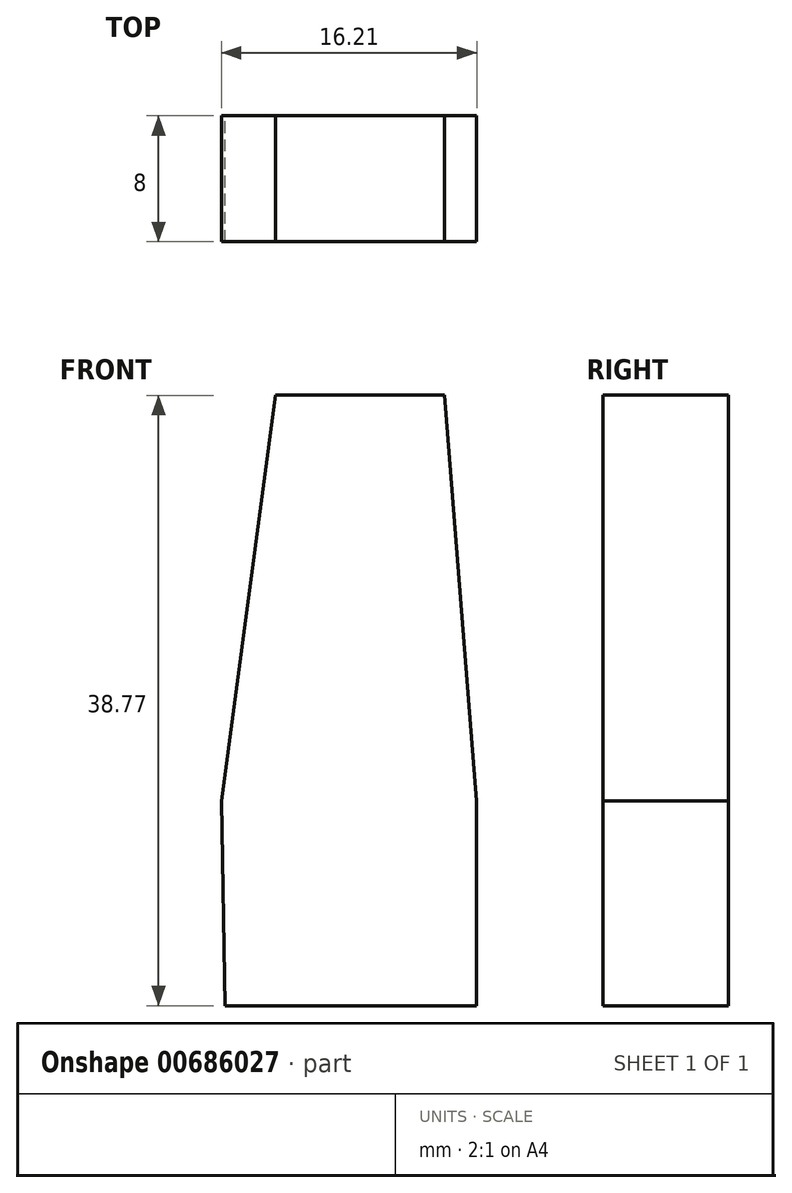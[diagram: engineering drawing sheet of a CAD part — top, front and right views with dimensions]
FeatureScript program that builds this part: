
annotation { "Feature Type Name" : "Feature", "Feature Type Description" : "" }
export const myFeature = defineFeature(function(context is Context, id is Id, definition is map)
    precondition{}
    {
        {
            var Q0;
            Q0=qCreatedBy(makeId("Front.planeOp"),FACE);
            var sketch = newSketch(context, id + "F0", { "sketchPlane" : qUnion([Q0])});
            skLineSegment(sketch, "E0", {"start": v(-7.82, 0) * mm, "end": v(8.18, 0) * mm});
            skLineSegment(sketch, "E1", {"start": v(8.18, 0) * mm, "end": v(8.18, 13) * mm});
            skLineSegment(sketch, "E2", {"start": v(8.18, 13) * mm, "end": v(6.14, 38.77) * mm});
            skLineSegment(sketch, "E3", {"start": v(6.14, 38.77) * mm, "end": v(-4.6, 38.77) * mm});
            skLineSegment(sketch, "E4", {"start": v(-4.6, 38.77) * mm, "end": v(-8.03, 13) * mm});
            skLineSegment(sketch, "E5", {"start": v(-8.03, 13) * mm, "end": v(-7.82, 0) * mm});
            skSolve(sketch);
        }
        {
            var Q0;
            Q0=makeQuery(id+"F0.imprint","IMPRINT",FACE,{"disambiguationData":[TD([[makeQuery(id+"F0.imprint","IMPRINT",EDGE,{"derivedFrom":sQuery(id+"F0.wireOp",EDGE,"E0")}),1.0]])]});
            extrude(context, id + "F1", {"entities" : qUnion([Q0]), "depth" : 8 * mm, "offsetDistance" : 25.4 * mm, "hasSecondDirection" : true, "secondDirectionOppositeDirection" : true, "secondDirectionDepth" : 8 * mm, "symmetric" : true});
        }
    });
